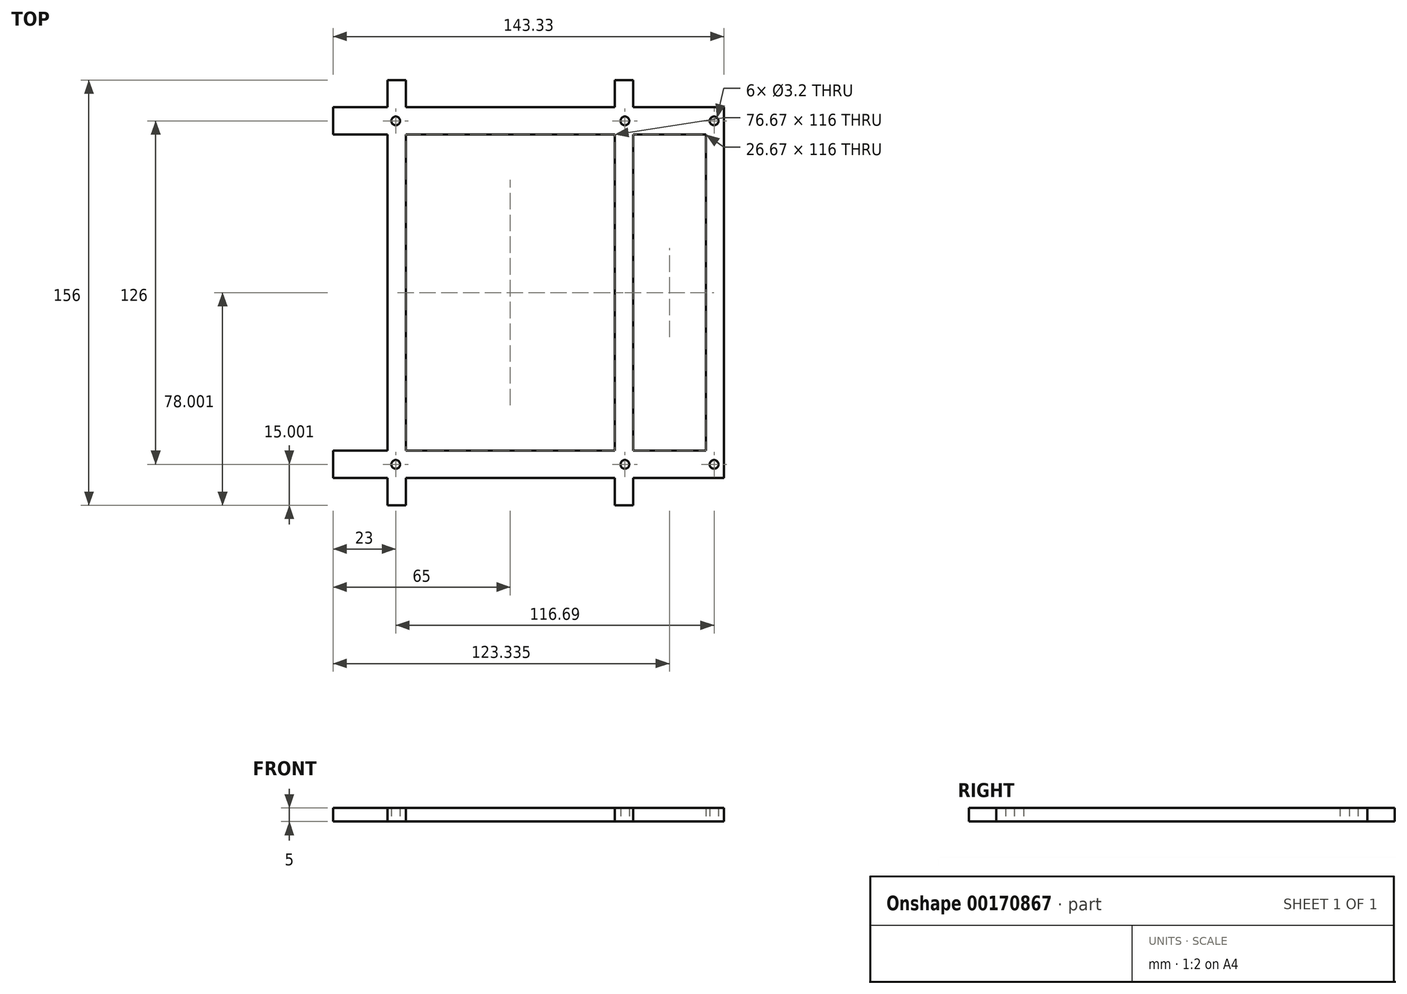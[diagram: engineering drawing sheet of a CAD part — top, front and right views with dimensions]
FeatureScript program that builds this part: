
annotation { "Feature Type Name" : "Feature", "Feature Type Description" : "" }
export const myFeature = defineFeature(function(context is Context, id is Id, definition is map)
    precondition{}
    {
        {
            var Q0;
            Q0=qCreatedBy(makeId("Top.planeOp"),FACE);
            var sketch = newSketch(context, id + "F0", { "sketchPlane" : qUnion([Q0])});
            skLineSegment(sketch, "E0.bottom", {"start": v(-16, 140.31) * mm, "end": v(94, 140.31) * mm});
            skLineSegment(sketch, "E0.top", {"start": v(-16, 340.31) * mm, "end": v(94, 340.31) * mm});
            skLineSegment(sketch, "E0.left", {"start": v(-16, 140.31) * mm, "end": v(-16, 340.31) * mm});
            skLineSegment(sketch, "E0.right", {"start": v(94, 140.31) * mm, "end": v(94, 340.31) * mm});
            skCircle(sketch, "E1", {"center": v(84, 328.31) * mm, "radius": 1.6 * mm});
            skCircle(sketch, "E2", {"center": v(0, 328.31) * mm, "radius": 1.6 * mm});
            skCircle(sketch, "E3", {"center": v(0, 202.31) * mm, "radius": 1.6 * mm});
            skCircle(sketch, "E4", {"center": v(84, 202.31) * mm, "radius": 1.6 * mm});
            skLineSegment(sketch, "E5", {"start": v(0, 328.31) * mm, "end": v(84, 328.31) * mm, "construction": true});
            skLineSegment(sketch, "E6", {"start": v(84, 202.31) * mm, "end": v(0, 202.31) * mm, "construction": true});
            skLineSegment(sketch, "E7", {"start": v(0, 202.31) * mm, "end": v(0, 328.31) * mm, "construction": true});
            skCircle(sketch, "E8", {"center": v(0, 328.31) * mm, "radius": 3 * mm, "construction": true});
            skCircle(sketch, "E9", {"center": v(84, 328.31) * mm, "radius": 3 * mm, "construction": true});
            skCircle(sketch, "E10", {"center": v(84, 202.31) * mm, "radius": 3 * mm, "construction": true});
            skCircle(sketch, "E11", {"center": v(0, 202.31) * mm, "radius": 3 * mm, "construction": true});
            skSolve(sketch);
        }
        {
            var Q0;
            Q0=qCreatedBy(makeId("Top.planeOp"),FACE);
            var sketch = newSketch(context, id + "F1", { "sketchPlane" : qUnion([Q0])});
            skCircle(sketch, "E12.0", {"center": v(0, 328.31) * mm, "radius": 1.6 * mm});
            skCircle(sketch, "E13.0", {"center": v(84, 328.31) * mm, "radius": 1.6 * mm});
            skCircle(sketch, "E14.0", {"center": v(0, 202.31) * mm, "radius": 1.6 * mm});
            skCircle(sketch, "E15.0", {"center": v(84, 202.31) * mm, "radius": 1.6 * mm});
            skLineSegment(sketch, "E16", {"start": v(0, 202.31) * mm, "end": v(84, 202.31) * mm, "construction": true});
            skLineSegment(sketch, "E17", {"start": v(-19.67, 187.31) * mm, "end": v(-19.67, 207.31) * mm, "construction": true});
            skLineSegment(sketch, "E18.0", {"start": v(-13, 187.31) * mm, "end": v(-13, 207.31) * mm, "construction": true});
            skLineSegment(sketch, "E19.1.0.0", {"start": v(3.67, 187.31) * mm, "end": v(3.67, 202.31) * mm});
            skLineSegment(sketch, "E19.1.0.1", {"start": v(-3, 187.31) * mm, "end": v(-3, 197.31) * mm});
            skLineSegment(sketch, "E19.6.0.0", {"start": v(87, 187.31) * mm, "end": v(87, 197.31) * mm});
            skLineSegment(sketch, "E19.6.0.1", {"start": v(80.33, 187.31) * mm, "end": v(80.33, 197.31) * mm});
            skLineSegment(sketch, "E19.direction1", {"start": v(-19.67, 187.31) * mm, "end": v(-3, 187.31) * mm, "construction": true});
            skLineSegment(sketch, "E20.0", {"start": v(-23, 197.31) * mm, "end": v(-23, 207.31) * mm});
            skLineSegment(sketch, "E21", {"start": v(-3, 225.2) * mm, "end": v(87, 225.2) * mm, "construction": true});
            skLineSegment(sketch, "E22", {"start": v(42, 225.2) * mm, "end": v(42, 202.31) * mm, "construction": true});
            skLineSegment(sketch, "E23.0.8.0", {"start": v(120.33, 197.31) * mm, "end": v(120.33, 333.31) * mm});
            skCircle(sketch, "E24.1.0.0", {"center": v(116.7, 202.31) * mm, "radius": 1.6 * mm});
            skCircle(sketch, "E24.1.0.1", {"center": v(116.7, 328.31) * mm, "radius": 1.6 * mm});
            skLineSegment(sketch, "E24.direction1", {"start": v(0, 202.31) * mm, "end": v(116.7, 202.31) * mm, "construction": true});
            skLineSegment(sketch, "E25", {"start": v(-3, 187.31) * mm, "end": v(3.67, 187.31) * mm});
            skLineSegment(sketch, "E26", {"start": v(-3, 343.31) * mm, "end": v(3.67, 343.31) * mm});
            skLineSegment(sketch, "E27", {"start": v(80.33, 343.31) * mm, "end": v(87, 343.31) * mm});
            skLineSegment(sketch, "E28", {"start": v(80.33, 187.31) * mm, "end": v(87, 187.31) * mm});
            skLineSegment(sketch, "E29", {"start": v(-23, 197.31) * mm, "end": v(-3, 197.31) * mm});
            skLineSegment(sketch, "E30.0", {"start": v(-23, 207.31) * mm, "end": v(-3, 207.31) * mm});
            skLineSegment(sketch, "E31", {"start": v(-23, 333.31) * mm, "end": v(-3, 333.31) * mm});
            skLineSegment(sketch, "E32.0", {"start": v(-23, 323.31) * mm, "end": v(-3, 323.31) * mm});
            skLineSegment(sketch, "E33.trimOffspring", {"start": v(-23, 323.31) * mm, "end": v(-23, 333.31) * mm});
            skLineSegment(sketch, "E34.trimOffspring", {"start": v(-19.67, 323.31) * mm, "end": v(-19.67, 343.31) * mm, "construction": true});
            skLineSegment(sketch, "E35.trimOffspring", {"start": v(-13, 323.31) * mm, "end": v(-13, 343.31) * mm, "construction": true});
            skLineSegment(sketch, "E36.trimOffspring", {"start": v(-3, 333.31) * mm, "end": v(-3, 343.31) * mm});
            skLineSegment(sketch, "E37.trimOffspring", {"start": v(3.67, 333.31) * mm, "end": v(80.33, 333.31) * mm});
            skLineSegment(sketch, "E38.trimOffspring", {"start": v(3.67, 333.31) * mm, "end": v(3.67, 343.31) * mm});
            skLineSegment(sketch, "E39.trimOffspring", {"start": v(3.67, 323.31) * mm, "end": v(80.33, 323.31) * mm});
            skLineSegment(sketch, "E40.trimOffspring", {"start": v(87, 333.31) * mm, "end": v(113.67, 333.31) * mm});
            skLineSegment(sketch, "E41.trimOffspring", {"start": v(87, 333.31) * mm, "end": v(87, 343.31) * mm});
            skLineSegment(sketch, "E42.trimOffspring", {"start": v(80.33, 333.31) * mm, "end": v(80.33, 343.31) * mm});
            skLineSegment(sketch, "E43.trimOffspring", {"start": v(87, 323.31) * mm, "end": v(113.67, 323.31) * mm});
            skLineSegment(sketch, "E44.trimOffspring", {"start": v(113.67, 207.31) * mm, "end": v(113.67, 323.31) * mm});
            skLineSegment(sketch, "E45.trimOffspring", {"start": v(87, 207.31) * mm, "end": v(113.67, 207.31) * mm});
            skLineSegment(sketch, "E46.trimOffspring", {"start": v(87, 207.31) * mm, "end": v(87, 323.31) * mm});
            skLineSegment(sketch, "E47.trimOffspring", {"start": v(87, 197.31) * mm, "end": v(113.67, 197.31) * mm});
            skLineSegment(sketch, "E48.trimOffspring", {"start": v(80.33, 207.31) * mm, "end": v(80.33, 323.31) * mm});
            skLineSegment(sketch, "E49.trimOffspring", {"start": v(3.67, 207.31) * mm, "end": v(3.67, 323.31) * mm});
            skLineSegment(sketch, "E50.trimOffspring", {"start": v(3.67, 207.31) * mm, "end": v(80.33, 207.31) * mm});
            skLineSegment(sketch, "E51.trimOffspring", {"start": v(-3, 207.31) * mm, "end": v(-3, 323.31) * mm});
            skLineSegment(sketch, "E52.trimOffspring", {"start": v(3.67, 197.31) * mm, "end": v(80.33, 197.31) * mm});
            skLineSegment(sketch, "E53", {"start": v(113.67, 333.31) * mm, "end": v(120.33, 333.31) * mm});
            skLineSegment(sketch, "E54", {"start": v(113.67, 197.31) * mm, "end": v(120.33, 197.31) * mm});
            skSolve(sketch);
        }
        {
            var Q0;
            Q0 = qSketchRegion(id + "F1", true);
            extrude(context, id + "F2", {"entities" : qUnion([Q0]), "depth" : 5 * mm});
        }
    });
